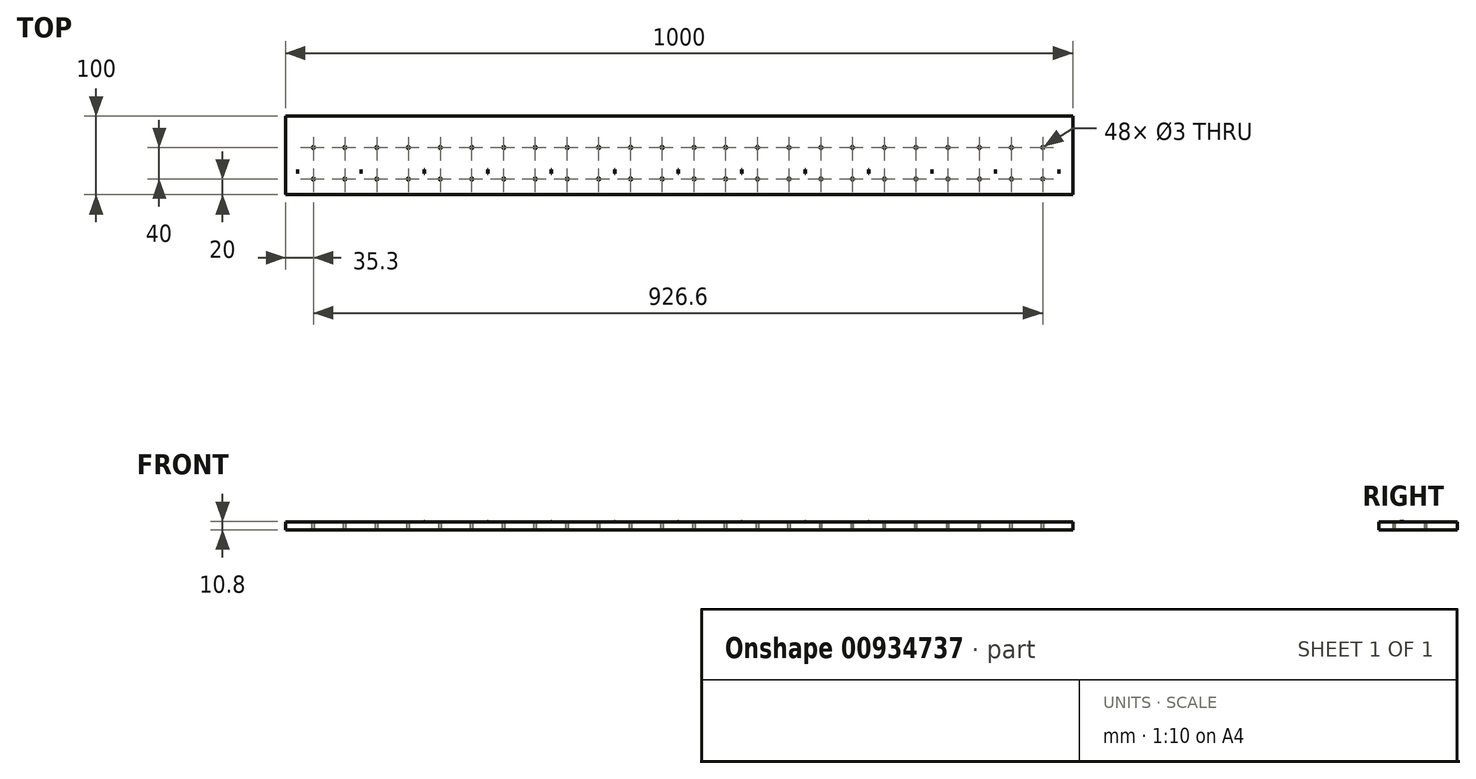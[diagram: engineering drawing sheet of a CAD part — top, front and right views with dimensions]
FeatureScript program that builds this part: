
annotation { "Feature Type Name" : "Feature", "Feature Type Description" : "" }
export const myFeature = defineFeature(function(context is Context, id is Id, definition is map)
    precondition{}
    {
        {
            var Q0;
            Q0=qCreatedBy(makeId("Top.planeOp"),FACE);
            var sketch = newSketch(context, id + "F0", { "sketchPlane" : qUnion([Q0])});
            skLineSegment(sketch, "E0.bottom", {"start": v(0, 0) * mm, "end": v(1000, 0) * mm});
            skLineSegment(sketch, "E0.top", {"start": v(0, 100) * mm, "end": v(1000, 100) * mm});
            skLineSegment(sketch, "E0.left", {"start": v(0, 0) * mm, "end": v(0, 100) * mm});
            skLineSegment(sketch, "E0.right", {"start": v(1000, 0) * mm, "end": v(1000, 100) * mm});
            skSolve(sketch);
        }
        {
            var Q0;
            Q0=makeQuery(id+"F0.imprint","IMPRINT",FACE,{"disambiguationData":[TD([[makeQuery(id+"F0.imprint","IMPRINT",EDGE,{"derivedFrom":sQuery(id+"F0.wireOp",EDGE,"E0.bottom")}),1.0]])]});
            extrude(context, id + "F1", {"entities" : qUnion([Q0]), "depth" : 10 * mm, "offsetDistance" : 25 * mm});
        }
        {
            var Q0;
            Q0=makeQuery(id+"F1.opExtrude","CAP_FACE",FACE,{"disambiguationData":[OSD([sQuery(id+"F0.wireOp",EDGE,"E0.bottom"),sQuery(id+"F0.wireOp",EDGE,"E0.top"),sQuery(id+"F0.wireOp",EDGE,"E0.left"),sQuery(id+"F0.wireOp",EDGE,"E0.right")])],"isStart":false});
            var sketch = newSketch(context, id + "F2", { "sketchPlane" : qUnion([Q0])});
            skLineSegment(sketch, "E1.bottom", {"start": v(15, 32) * mm, "end": v(15.3, 32) * mm});
            skLineSegment(sketch, "E1.top", {"start": v(15, 27) * mm, "end": v(15.3, 27) * mm});
            skLineSegment(sketch, "E1.left", {"start": v(15, 32) * mm, "end": v(15, 27) * mm});
            skLineSegment(sketch, "E1.right", {"start": v(15.3, 32) * mm, "end": v(15.3, 27) * mm});
            skLineSegment(sketch, "E2.1.0.0", {"start": v(95.6, 27) * mm, "end": v(95.9, 27) * mm});
            skLineSegment(sketch, "E2.1.0.1", {"start": v(95.9, 32) * mm, "end": v(95.9, 27) * mm});
            skLineSegment(sketch, "E2.1.0.2", {"start": v(95.6, 32) * mm, "end": v(95.6, 27) * mm});
            skLineSegment(sketch, "E2.1.0.3", {"start": v(95.6, 32) * mm, "end": v(95.9, 32) * mm});
            skLineSegment(sketch, "E2.2.0.0", {"start": v(176.2, 27) * mm, "end": v(176.5, 27) * mm});
            skLineSegment(sketch, "E2.2.0.1", {"start": v(176.5, 32) * mm, "end": v(176.5, 27) * mm});
            skLineSegment(sketch, "E2.2.0.2", {"start": v(176.2, 32) * mm, "end": v(176.2, 27) * mm});
            skLineSegment(sketch, "E2.2.0.3", {"start": v(176.2, 32) * mm, "end": v(176.5, 32) * mm});
            skLineSegment(sketch, "E2.3.0.0", {"start": v(256.8, 27) * mm, "end": v(257.1, 27) * mm});
            skLineSegment(sketch, "E2.3.0.1", {"start": v(257.1, 32) * mm, "end": v(257.1, 27) * mm});
            skLineSegment(sketch, "E2.3.0.2", {"start": v(256.8, 32) * mm, "end": v(256.8, 27) * mm});
            skLineSegment(sketch, "E2.3.0.3", {"start": v(256.8, 32) * mm, "end": v(257.1, 32) * mm});
            skLineSegment(sketch, "E2.4.0.0", {"start": v(337.4, 27) * mm, "end": v(337.7, 27) * mm});
            skLineSegment(sketch, "E2.4.0.1", {"start": v(337.7, 32) * mm, "end": v(337.7, 27) * mm});
            skLineSegment(sketch, "E2.4.0.2", {"start": v(337.4, 32) * mm, "end": v(337.4, 27) * mm});
            skLineSegment(sketch, "E2.4.0.3", {"start": v(337.4, 32) * mm, "end": v(337.7, 32) * mm});
            skLineSegment(sketch, "E2.5.0.0", {"start": v(418, 27) * mm, "end": v(418.3, 27) * mm});
            skLineSegment(sketch, "E2.5.0.1", {"start": v(418.3, 32) * mm, "end": v(418.3, 27) * mm});
            skLineSegment(sketch, "E2.5.0.2", {"start": v(418, 32) * mm, "end": v(418, 27) * mm});
            skLineSegment(sketch, "E2.5.0.3", {"start": v(418, 32) * mm, "end": v(418.3, 32) * mm});
            skLineSegment(sketch, "E2.6.0.0", {"start": v(498.6, 27) * mm, "end": v(498.9, 27) * mm});
            skLineSegment(sketch, "E2.6.0.1", {"start": v(498.9, 32) * mm, "end": v(498.9, 27) * mm});
            skLineSegment(sketch, "E2.6.0.2", {"start": v(498.6, 32) * mm, "end": v(498.6, 27) * mm});
            skLineSegment(sketch, "E2.6.0.3", {"start": v(498.6, 32) * mm, "end": v(498.9, 32) * mm});
            skLineSegment(sketch, "E2.7.0.0", {"start": v(579.2, 27) * mm, "end": v(579.5, 27) * mm});
            skLineSegment(sketch, "E2.7.0.1", {"start": v(579.5, 32) * mm, "end": v(579.5, 27) * mm});
            skLineSegment(sketch, "E2.7.0.2", {"start": v(579.2, 32) * mm, "end": v(579.2, 27) * mm});
            skLineSegment(sketch, "E2.7.0.3", {"start": v(579.2, 32) * mm, "end": v(579.5, 32) * mm});
            skLineSegment(sketch, "E2.8.0.0", {"start": v(659.8, 27) * mm, "end": v(660.1, 27) * mm});
            skLineSegment(sketch, "E2.8.0.1", {"start": v(660.1, 32) * mm, "end": v(660.1, 27) * mm});
            skLineSegment(sketch, "E2.8.0.2", {"start": v(659.8, 32) * mm, "end": v(659.8, 27) * mm});
            skLineSegment(sketch, "E2.8.0.3", {"start": v(659.8, 32) * mm, "end": v(660.1, 32) * mm});
            skLineSegment(sketch, "E2.9.0.0", {"start": v(740.4, 27) * mm, "end": v(740.7, 27) * mm});
            skLineSegment(sketch, "E2.9.0.1", {"start": v(740.7, 32) * mm, "end": v(740.7, 27) * mm});
            skLineSegment(sketch, "E2.9.0.2", {"start": v(740.4, 32) * mm, "end": v(740.4, 27) * mm});
            skLineSegment(sketch, "E2.9.0.3", {"start": v(740.4, 32) * mm, "end": v(740.7, 32) * mm});
            skLineSegment(sketch, "E2.10.0.0", {"start": v(821, 27) * mm, "end": v(821.3, 27) * mm});
            skLineSegment(sketch, "E2.10.0.1", {"start": v(821.3, 32) * mm, "end": v(821.3, 27) * mm});
            skLineSegment(sketch, "E2.10.0.2", {"start": v(821, 32) * mm, "end": v(821, 27) * mm});
            skLineSegment(sketch, "E2.10.0.3", {"start": v(821, 32) * mm, "end": v(821.3, 32) * mm});
            skLineSegment(sketch, "E2.11.0.0", {"start": v(901.6, 27) * mm, "end": v(901.9, 27) * mm});
            skLineSegment(sketch, "E2.11.0.1", {"start": v(901.9, 32) * mm, "end": v(901.9, 27) * mm});
            skLineSegment(sketch, "E2.11.0.2", {"start": v(901.6, 32) * mm, "end": v(901.6, 27) * mm});
            skLineSegment(sketch, "E2.11.0.3", {"start": v(901.6, 32) * mm, "end": v(901.9, 32) * mm});
            skLineSegment(sketch, "E2.12.0.0", {"start": v(982.2, 27) * mm, "end": v(982.5, 27) * mm});
            skLineSegment(sketch, "E2.12.0.1", {"start": v(982.5, 32) * mm, "end": v(982.5, 27) * mm});
            skLineSegment(sketch, "E2.12.0.2", {"start": v(982.2, 32) * mm, "end": v(982.2, 27) * mm});
            skLineSegment(sketch, "E2.12.0.3", {"start": v(982.2, 32) * mm, "end": v(982.5, 32) * mm});
            skLineSegment(sketch, "E2.direction1", {"start": v(15, 27) * mm, "end": v(95.6, 27) * mm, "construction": true});
            skSolve(sketch);
        }
        {
            var Q0;
            Q0 = qSketchRegion(id + "F2", true);
            extrude(context, id + "F3", {"entities" : qUnion([Q0]), "operationType" : NewBodyOperationType.ADD, "depth" : 0.8 * mm, "offsetDistance" : 25 * mm});
        }
        {
            var Q0;
            Q0=makeQuery(id+"F1.opExtrude","CAP_FACE",FACE,{"disambiguationData":[OSD([sQuery(id+"F0.wireOp",EDGE,"E0.bottom"),sQuery(id+"F0.wireOp",EDGE,"E0.top"),sQuery(id+"F0.wireOp",EDGE,"E0.left"),sQuery(id+"F0.wireOp",EDGE,"E0.right")])],"isStart":false});
            var sketch = newSketch(context, id + "F4", { "sketchPlane" : qUnion([Q0])});
            skCircle(sketch, "E3", {"center": v(35.3, 20) * mm, "radius": 1.5 * mm});
            skCircle(sketch, "E4", {"center": v(75.3, 20) * mm, "radius": 1.5 * mm});
            skCircle(sketch, "E5", {"center": v(35.3, 60) * mm, "radius": 1.5 * mm});
            skCircle(sketch, "E6", {"center": v(75.3, 60) * mm, "radius": 1.5 * mm});
            skCircle(sketch, "E7.1.0.0", {"center": v(115.9, 20) * mm, "radius": 1.5 * mm});
            skCircle(sketch, "E7.1.0.1", {"center": v(115.9, 60) * mm, "radius": 1.5 * mm});
            skCircle(sketch, "E7.1.0.2", {"center": v(155.9, 60) * mm, "radius": 1.5 * mm});
            skCircle(sketch, "E7.1.0.3", {"center": v(155.9, 20) * mm, "radius": 1.5 * mm});
            skCircle(sketch, "E7.2.0.0", {"center": v(196.5, 20) * mm, "radius": 1.5 * mm});
            skCircle(sketch, "E7.2.0.1", {"center": v(196.5, 60) * mm, "radius": 1.5 * mm});
            skCircle(sketch, "E7.2.0.2", {"center": v(236.5, 60) * mm, "radius": 1.5 * mm});
            skCircle(sketch, "E7.2.0.3", {"center": v(236.5, 20) * mm, "radius": 1.5 * mm});
            skCircle(sketch, "E7.3.0.0", {"center": v(277.1, 20) * mm, "radius": 1.5 * mm});
            skCircle(sketch, "E7.3.0.1", {"center": v(277.1, 60) * mm, "radius": 1.5 * mm});
            skCircle(sketch, "E7.3.0.2", {"center": v(317.1, 60) * mm, "radius": 1.5 * mm});
            skCircle(sketch, "E7.3.0.3", {"center": v(317.1, 20) * mm, "radius": 1.5 * mm});
            skCircle(sketch, "E7.4.0.0", {"center": v(357.7, 20) * mm, "radius": 1.5 * mm});
            skCircle(sketch, "E7.4.0.1", {"center": v(357.7, 60) * mm, "radius": 1.5 * mm});
            skCircle(sketch, "E7.4.0.2", {"center": v(397.7, 60) * mm, "radius": 1.5 * mm});
            skCircle(sketch, "E7.4.0.3", {"center": v(397.7, 20) * mm, "radius": 1.5 * mm});
            skCircle(sketch, "E7.5.0.0", {"center": v(438.3, 20) * mm, "radius": 1.5 * mm});
            skCircle(sketch, "E7.5.0.1", {"center": v(438.3, 60) * mm, "radius": 1.5 * mm});
            skCircle(sketch, "E7.5.0.2", {"center": v(478.3, 60) * mm, "radius": 1.5 * mm});
            skCircle(sketch, "E7.5.0.3", {"center": v(478.3, 20) * mm, "radius": 1.5 * mm});
            skCircle(sketch, "E7.6.0.0", {"center": v(518.9, 20) * mm, "radius": 1.5 * mm});
            skCircle(sketch, "E7.6.0.1", {"center": v(518.9, 60) * mm, "radius": 1.5 * mm});
            skCircle(sketch, "E7.6.0.2", {"center": v(558.9, 60) * mm, "radius": 1.5 * mm});
            skCircle(sketch, "E7.6.0.3", {"center": v(558.9, 20) * mm, "radius": 1.5 * mm});
            skCircle(sketch, "E7.7.0.0", {"center": v(599.5, 20) * mm, "radius": 1.5 * mm});
            skCircle(sketch, "E7.7.0.1", {"center": v(599.5, 60) * mm, "radius": 1.5 * mm});
            skCircle(sketch, "E7.7.0.2", {"center": v(639.5, 60) * mm, "radius": 1.5 * mm});
            skCircle(sketch, "E7.7.0.3", {"center": v(639.5, 20) * mm, "radius": 1.5 * mm});
            skCircle(sketch, "E7.8.0.0", {"center": v(680.1, 20) * mm, "radius": 1.5 * mm});
            skCircle(sketch, "E7.8.0.1", {"center": v(680.1, 60) * mm, "radius": 1.5 * mm});
            skCircle(sketch, "E7.8.0.2", {"center": v(720.1, 60) * mm, "radius": 1.5 * mm});
            skCircle(sketch, "E7.8.0.3", {"center": v(720.1, 20) * mm, "radius": 1.5 * mm});
            skCircle(sketch, "E7.9.0.0", {"center": v(760.7, 20) * mm, "radius": 1.5 * mm});
            skCircle(sketch, "E7.9.0.1", {"center": v(760.7, 60) * mm, "radius": 1.5 * mm});
            skCircle(sketch, "E7.9.0.2", {"center": v(800.7, 60) * mm, "radius": 1.5 * mm});
            skCircle(sketch, "E7.9.0.3", {"center": v(800.7, 20) * mm, "radius": 1.5 * mm});
            skCircle(sketch, "E7.10.0.0", {"center": v(841.3, 20) * mm, "radius": 1.5 * mm});
            skCircle(sketch, "E7.10.0.1", {"center": v(841.3, 60) * mm, "radius": 1.5 * mm});
            skCircle(sketch, "E7.10.0.2", {"center": v(881.3, 60) * mm, "radius": 1.5 * mm});
            skCircle(sketch, "E7.10.0.3", {"center": v(881.3, 20) * mm, "radius": 1.5 * mm});
            skCircle(sketch, "E7.11.0.0", {"center": v(921.9, 20) * mm, "radius": 1.5 * mm});
            skCircle(sketch, "E7.11.0.1", {"center": v(921.9, 60) * mm, "radius": 1.5 * mm});
            skCircle(sketch, "E7.11.0.2", {"center": v(961.9, 60) * mm, "radius": 1.5 * mm});
            skCircle(sketch, "E7.11.0.3", {"center": v(961.9, 20) * mm, "radius": 1.5 * mm});
            skLineSegment(sketch, "E7.direction1", {"start": v(35.3, 20) * mm, "end": v(115.9, 20) * mm, "construction": true});
            skSolve(sketch);
        }
        {
            var Q0;
            Q0 = qSketchRegion(id + "F4", true);
            extrude(context, id + "F5", {"entities" : qUnion([Q0]), "operationType" : NewBodyOperationType.REMOVE, "endBound" : BoundingType.THROUGH_ALL, "oppositeDirection" : true, "depth" : 25 * mm, "offsetDistance" : 25 * mm});
        }
    });
